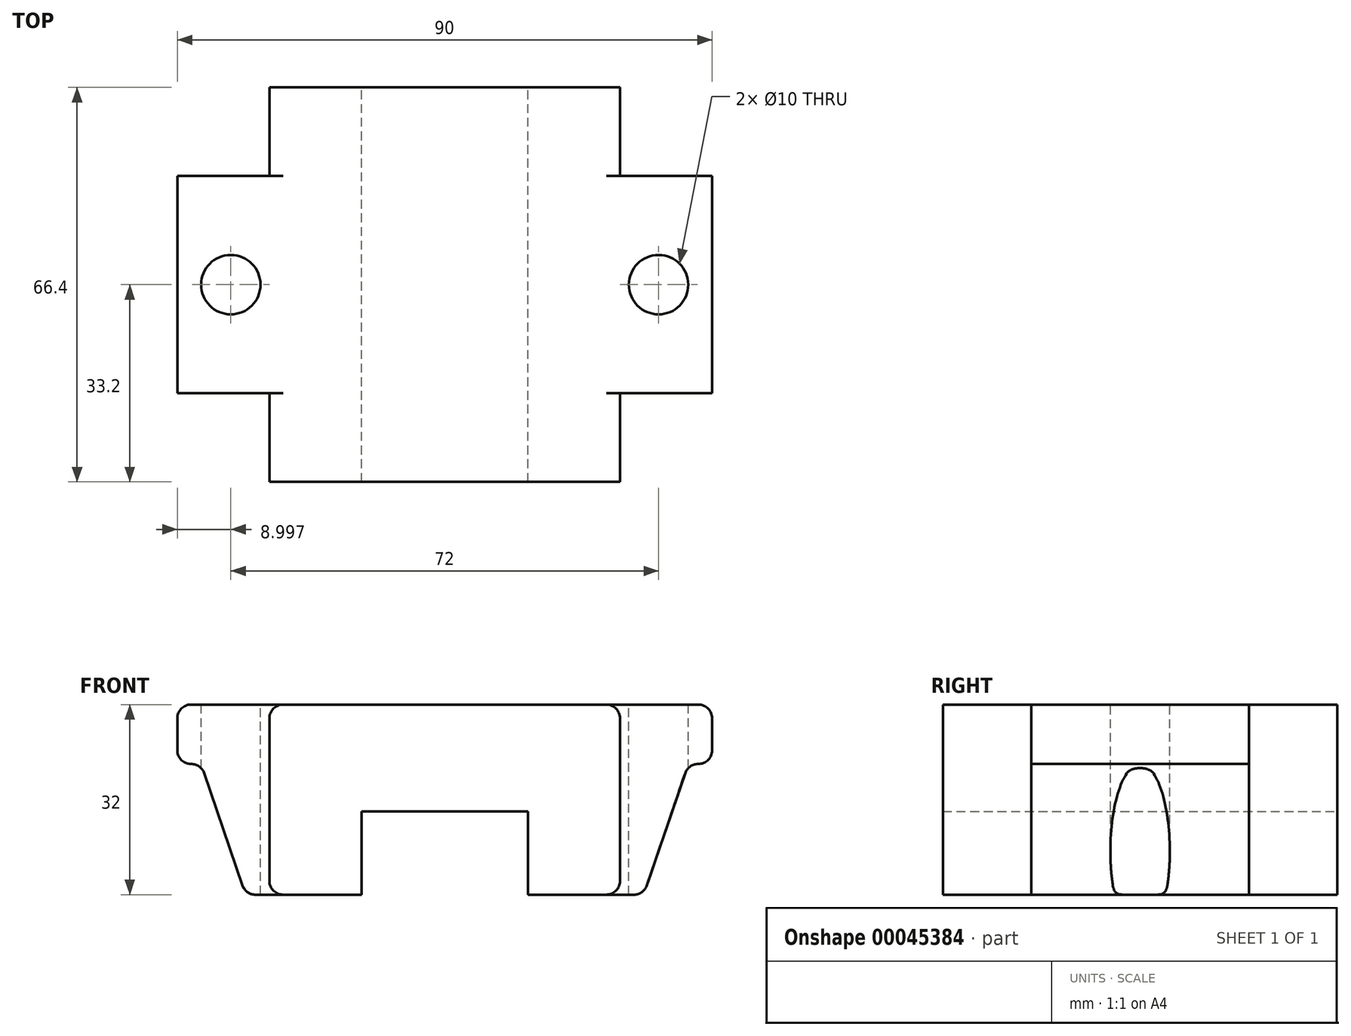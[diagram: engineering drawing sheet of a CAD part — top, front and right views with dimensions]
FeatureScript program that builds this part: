
annotation { "Feature Type Name" : "Feature", "Feature Type Description" : "" }
export const myFeature = defineFeature(function(context is Context, id is Id, definition is map)
    precondition{}
    {
        {
            var Q0;
            Q0=qCreatedBy(makeId("Front.planeOp"),FACE);
            var sketch = newSketch(context, id + "F0", { "sketchPlane" : qUnion([Q0])});
            skLineSegment(sketch, "E0.bottom", {"start": v(-43.91, 8.76) * mm, "end": v(46.09, 8.76) * mm});
            skLineSegment(sketch, "E0.top", {"start": v(-32.41, -23.24) * mm, "end": v(-12.91, -23.24) * mm});
            skLineSegment(sketch, "E0.left", {"start": v(-43.91, 8.76) * mm, "end": v(-43.91, -1.24) * mm});
            skLineSegment(sketch, "E0.right", {"start": v(46.09, 8.76) * mm, "end": v(46.09, -1.24) * mm});
            skLineSegment(sketch, "E1.top", {"start": v(-43.91, -1.24) * mm, "end": v(-39.91, -1.24) * mm});
            skLineSegment(sketch, "E2.bottom", {"start": v(-28.41, 8.76) * mm, "end": v(30.59, 8.76) * mm});
            skLineSegment(sketch, "E2.top", {"start": v(-28.41, -23.24) * mm, "end": v(-12.91, -23.24) * mm});
            skLineSegment(sketch, "E2.left", {"start": v(-28.41, 8.76) * mm, "end": v(-28.41, -23.24) * mm});
            skLineSegment(sketch, "E2.right", {"start": v(30.59, 8.76) * mm, "end": v(30.59, -23.24) * mm});
            skLineSegment(sketch, "E3.top", {"start": v(-12.91, -9.24) * mm, "end": v(15.09, -9.24) * mm});
            skLineSegment(sketch, "E3.left", {"start": v(-12.91, -23.24) * mm, "end": v(-12.91, -9.24) * mm});
            skLineSegment(sketch, "E3.right", {"start": v(15.09, -23.24) * mm, "end": v(15.09, -9.24) * mm});
            skLineSegment(sketch, "E4.trimOffspring", {"start": v(15.09, -23.24) * mm, "end": v(30.59, -23.24) * mm});
            skLineSegment(sketch, "E5.trimOffspring", {"start": v(15.09, -23.24) * mm, "end": v(34.59, -23.24) * mm});
            skLineSegment(sketch, "E6", {"start": v(-39.91, -1.24) * mm, "end": v(-32.41, -23.24) * mm});
            skLineSegment(sketch, "E7", {"start": v(34.59, -23.24) * mm, "end": v(42.09, -1.24) * mm});
            skLineSegment(sketch, "E8.trimOffspring", {"start": v(42.09, -1.24) * mm, "end": v(46.09, -1.24) * mm});
            skSolve(sketch);
        }
        {
            var Q0;
            Q0 = qSketchRegion(id + "F0", true);
            extrude(context, id + "F1", {"entities" : qUnion([Q0]), "depth" : 36.6 * mm});
        }
        {
            var Q0;
            Q0=makeQuery(id+"F1.opExtrude","CAP_FACE",FACE,{"disambiguationData":[OSD([sQuery(id+"F0.wireOp",EDGE,"E0.top"),sQuery(id+"F0.wireOp",EDGE,"E0.bottom"),sQuery(id+"F0.wireOp",EDGE,"E1.top"),sQuery(id+"F0.wireOp",EDGE,"E0.left"),sQuery(id+"F0.wireOp",EDGE,"E0.right"),sQuery(id+"F0.wireOp",EDGE,"E2.bottom"),sQuery(id+"F0.wireOp",EDGE,"E2.top"),sQuery(id+"F0.wireOp",EDGE,"E3.top"),sQuery(id+"F0.wireOp",EDGE,"E3.left"),sQuery(id+"F0.wireOp",EDGE,"E3.right"),sQuery(id+"F0.wireOp",EDGE,"E5.trimOffspring"),sQuery(id+"F0.wireOp",EDGE,"E6"),sQuery(id+"F0.wireOp",EDGE,"E7"),sQuery(id+"F0.wireOp",EDGE,"E8.trimOffspring")])],"isStart":true});
            var sketch = newSketch(context, id + "F2", { "sketchPlane" : qUnion([Q0])});
            skLineSegment(sketch, "E9.top", {"start": v(-30.59, 8.76) * mm, "end": v(28.41, 8.76) * mm});
            skLineSegment(sketch, "E9.left", {"start": v(-30.59, -23.24) * mm, "end": v(-30.59, 8.76) * mm});
            skLineSegment(sketch, "E9.right", {"start": v(28.41, -23.24) * mm, "end": v(28.41, 8.76) * mm});
            skLineSegment(sketch, "E10.top", {"start": v(-15.09, -9.24) * mm, "end": v(12.91, -9.24) * mm});
            skLineSegment(sketch, "E10.left", {"start": v(-15.09, -23.24) * mm, "end": v(-15.09, -9.24) * mm});
            skLineSegment(sketch, "E10.right", {"start": v(12.91, -23.24) * mm, "end": v(12.91, -9.24) * mm});
            skLineSegment(sketch, "E11.trimOffspring", {"start": v(12.91, -23.24) * mm, "end": v(28.41, -23.24) * mm});
            skLineSegment(sketch, "E12", {"start": v(-30.59, -23.24) * mm, "end": v(-15.09, -23.24) * mm});
            skSolve(sketch);
        }
        {
            var Q0;
            Q0 = qSketchRegion(id + "F2", true);
            extrude(context, id + "F3", {"entities" : qUnion([Q0]), "operationType" : NewBodyOperationType.ADD, "depth" : 14.9 * mm, "hasSecondDirection" : true, "secondDirectionOppositeDirection" : true, "secondDirectionDepth" : 51.5 * mm});
        }
        {
            var Q0;
            Q0=makeQuery(id+"F3.boolean.opBoolean","MERGE",FACE,{"derivedFrom":[makeQuery(id+"F1.opExtrude","SWEPT_FACE",FACE,{"disambiguationData":[OSD([sQuery(id+"F0.wireOp",EDGE,"E0.bottom"),sQuery(id+"F0.wireOp",EDGE,"E2.bottom")])]}),makeQuery(id+"F3.opExtrude","SWEPT_FACE",FACE,{"disambiguationData":[OSD([sQuery(id+"F2.wireOp",EDGE,"E9.top")])]})]});
            var sketch = newSketch(context, id + "F4", { "sketchPlane" : qUnion([Q0])});
            skCircle(sketch, "E13", {"center": v(-34.91, -18.3) * mm, "radius": 5 * mm});
            skCircle(sketch, "E14", {"center": v(37.09, -18.3) * mm, "radius": 5 * mm});
            skSolve(sketch);
        }
        {
            var Q0;
            Q0 = qSketchRegion(id + "F4", true);
            extrude(context, id + "F5", {"entities" : qUnion([Q0]), "operationType" : NewBodyOperationType.REMOVE, "endBound" : BoundingType.THROUGH_ALL, "oppositeDirection" : true, "depth" : 25 * mm});
        }
        {
            var Q0;
            {var subQ0=sQuery(id+"F0.wireOp",EDGE,"E6");var subQ1=sQuery(id+"F0.wireOp",EDGE,"E1.top");Q0=makeQuery(id+"F5.boolean.opBoolean","SPLIT",EDGE,{"disambiguationData":[TD([makeQuery(id+"F1.opExtrude","CAP_FACE",FACE,{"disambiguationData":[OSD([sQuery(id+"F0.wireOp",EDGE,"E0.top"),sQuery(id+"F0.wireOp",EDGE,"E0.bottom"),subQ1,sQuery(id+"F0.wireOp",EDGE,"E0.left"),sQuery(id+"F0.wireOp",EDGE,"E0.right"),sQuery(id+"F0.wireOp",EDGE,"E2.bottom"),sQuery(id+"F0.wireOp",EDGE,"E2.top"),sQuery(id+"F0.wireOp",EDGE,"E3.top"),sQuery(id+"F0.wireOp",EDGE,"E3.left"),sQuery(id+"F0.wireOp",EDGE,"E3.right"),sQuery(id+"F0.wireOp",EDGE,"E5.trimOffspring"),subQ0,sQuery(id+"F0.wireOp",EDGE,"E7"),sQuery(id+"F0.wireOp",EDGE,"E8.trimOffspring")])],"isStart":false})])],"derivedFrom":makeQuery(id+"F1.opExtrude","SWEPT_EDGE",EDGE,{"disambiguationData":[OSD([subQ1,subQ0])]})});}
            var Q1;
            Q1=makeQuery(id+"F1.opExtrude","SWEPT_EDGE",EDGE,{"disambiguationData":[OSD([sQuery(id+"F0.wireOp",EDGE,"E1.top"),sQuery(id+"F0.wireOp",EDGE,"E0.left")])]});
            var Q2;
            Q2=makeQuery(id+"F1.opExtrude","SWEPT_EDGE",EDGE,{"disambiguationData":[OSD([sQuery(id+"F0.wireOp",EDGE,"E0.bottom"),sQuery(id+"F0.wireOp",EDGE,"E0.left")])]});
            var Q3;
            {var subQ0=sQuery(id+"F0.wireOp",EDGE,"E6");var subQ1=sQuery(id+"F0.wireOp",EDGE,"E2.top");var subQ2=sQuery(id+"F0.wireOp",EDGE,"E0.top");Q3=makeQuery(id+"F5.boolean.opBoolean","SPLIT",EDGE,{"disambiguationData":[TD([makeQuery(id+"F1.opExtrude","CAP_FACE",FACE,{"disambiguationData":[OSD([subQ2,sQuery(id+"F0.wireOp",EDGE,"E0.bottom"),sQuery(id+"F0.wireOp",EDGE,"E1.top"),sQuery(id+"F0.wireOp",EDGE,"E0.left"),sQuery(id+"F0.wireOp",EDGE,"E0.right"),sQuery(id+"F0.wireOp",EDGE,"E2.bottom"),subQ1,sQuery(id+"F0.wireOp",EDGE,"E3.top"),sQuery(id+"F0.wireOp",EDGE,"E3.left"),sQuery(id+"F0.wireOp",EDGE,"E3.right"),sQuery(id+"F0.wireOp",EDGE,"E5.trimOffspring"),subQ0,sQuery(id+"F0.wireOp",EDGE,"E7"),sQuery(id+"F0.wireOp",EDGE,"E8.trimOffspring")])],"isStart":false})])],"derivedFrom":makeQuery(id+"F1.opExtrude","SWEPT_EDGE",EDGE,{"disambiguationData":[OSD([subQ2,subQ0])]})});}
            var Q4;
            {var subQ0=sQuery(id+"F0.wireOp",EDGE,"E6");var subQ1=sQuery(id+"F0.wireOp",EDGE,"E2.top");var subQ2=sQuery(id+"F0.wireOp",EDGE,"E0.top");Q4=makeQuery(id+"F5.boolean.opBoolean","SPLIT",EDGE,{"disambiguationData":[TD([makeQuery(id+"F1.opExtrude","CAP_FACE",FACE,{"disambiguationData":[OSD([subQ2,sQuery(id+"F0.wireOp",EDGE,"E0.bottom"),sQuery(id+"F0.wireOp",EDGE,"E1.top"),sQuery(id+"F0.wireOp",EDGE,"E0.left"),sQuery(id+"F0.wireOp",EDGE,"E0.right"),sQuery(id+"F0.wireOp",EDGE,"E2.bottom"),subQ1,sQuery(id+"F0.wireOp",EDGE,"E3.top"),sQuery(id+"F0.wireOp",EDGE,"E3.left"),sQuery(id+"F0.wireOp",EDGE,"E3.right"),sQuery(id+"F0.wireOp",EDGE,"E5.trimOffspring"),subQ0,sQuery(id+"F0.wireOp",EDGE,"E7"),sQuery(id+"F0.wireOp",EDGE,"E8.trimOffspring")])],"isStart":true})])],"derivedFrom":makeQuery(id+"F1.opExtrude","SWEPT_EDGE",EDGE,{"disambiguationData":[OSD([subQ2,subQ0])]})});}
            var Q5;
            {var subQ0=sQuery(id+"F2.wireOp",EDGE,"E9.right");var subQ1=sQuery(id+"F0.wireOp",EDGE,"E2.top");var subQ2=sQuery(id+"F0.wireOp",EDGE,"E0.top");var subQ3=sQuery(id+"F2.wireOp",EDGE,"E11.trimOffspring");Q5=makeQuery(id+"F3.boolean.opBoolean","SPLIT",EDGE,{"disambiguationData":[TD([makeQuery(id+"F3.opExtrude","CAP_FACE",FACE,{"disambiguationData":[OSD([sQuery(id+"F2.wireOp",EDGE,"E9.top"),sQuery(id+"F2.wireOp",EDGE,"E9.left"),subQ0,sQuery(id+"F2.wireOp",EDGE,"E10.top"),sQuery(id+"F2.wireOp",EDGE,"E10.left"),sQuery(id+"F2.wireOp",EDGE,"E10.right"),subQ3,sQuery(id+"F2.wireOp",EDGE,"E12")])],"isStart":true})])],"derivedFrom":makeQuery(id+"F3.opExtrude","SWEPT_EDGE",EDGE,{"disambiguationData":[OSD([subQ2,subQ1,subQ0,subQ3])]})});}
            var Q6;
            {var subQ0=sQuery(id+"F2.wireOp",EDGE,"E9.right");var subQ1=sQuery(id+"F0.wireOp",EDGE,"E2.top");var subQ2=sQuery(id+"F0.wireOp",EDGE,"E0.top");var subQ3=sQuery(id+"F2.wireOp",EDGE,"E11.trimOffspring");Q6=makeQuery(id+"F3.boolean.opBoolean","SPLIT",EDGE,{"disambiguationData":[TD([makeQuery(id+"F3.opExtrude","CAP_FACE",FACE,{"disambiguationData":[OSD([sQuery(id+"F2.wireOp",EDGE,"E9.top"),sQuery(id+"F2.wireOp",EDGE,"E9.left"),subQ0,sQuery(id+"F2.wireOp",EDGE,"E10.top"),sQuery(id+"F2.wireOp",EDGE,"E10.left"),sQuery(id+"F2.wireOp",EDGE,"E10.right"),subQ3,sQuery(id+"F2.wireOp",EDGE,"E12")])],"isStart":false})])],"derivedFrom":makeQuery(id+"F3.opExtrude","SWEPT_EDGE",EDGE,{"disambiguationData":[OSD([subQ2,subQ1,subQ0,subQ3])]})});}
            var Q7;
            {var subQ0=sQuery(id+"F0.wireOp",EDGE,"E2.bottom");var subQ1=sQuery(id+"F0.wireOp",EDGE,"E0.bottom");var subQ2=sQuery(id+"F2.wireOp",EDGE,"E9.right");var subQ3=sQuery(id+"F2.wireOp",EDGE,"E9.top");Q7=makeQuery(id+"F3.boolean.opBoolean","SPLIT",EDGE,{"disambiguationData":[TD([makeQuery(id+"F3.opExtrude","CAP_FACE",FACE,{"disambiguationData":[OSD([subQ3,sQuery(id+"F2.wireOp",EDGE,"E9.left"),subQ2,sQuery(id+"F2.wireOp",EDGE,"E10.top"),sQuery(id+"F2.wireOp",EDGE,"E10.left"),sQuery(id+"F2.wireOp",EDGE,"E10.right"),sQuery(id+"F2.wireOp",EDGE,"E11.trimOffspring"),sQuery(id+"F2.wireOp",EDGE,"E12")])],"isStart":true})])],"derivedFrom":makeQuery(id+"F3.opExtrude","SWEPT_EDGE",EDGE,{"disambiguationData":[OSD([subQ1,subQ0,subQ3,subQ2])]})});}
            var Q8;
            {var subQ0=sQuery(id+"F0.wireOp",EDGE,"E2.bottom");var subQ1=sQuery(id+"F0.wireOp",EDGE,"E0.bottom");var subQ2=sQuery(id+"F2.wireOp",EDGE,"E9.right");var subQ3=sQuery(id+"F2.wireOp",EDGE,"E9.top");Q8=makeQuery(id+"F3.boolean.opBoolean","SPLIT",EDGE,{"disambiguationData":[TD([makeQuery(id+"F3.opExtrude","CAP_FACE",FACE,{"disambiguationData":[OSD([subQ3,sQuery(id+"F2.wireOp",EDGE,"E9.left"),subQ2,sQuery(id+"F2.wireOp",EDGE,"E10.top"),sQuery(id+"F2.wireOp",EDGE,"E10.left"),sQuery(id+"F2.wireOp",EDGE,"E10.right"),sQuery(id+"F2.wireOp",EDGE,"E11.trimOffspring"),sQuery(id+"F2.wireOp",EDGE,"E12")])],"isStart":false})])],"derivedFrom":makeQuery(id+"F3.opExtrude","SWEPT_EDGE",EDGE,{"disambiguationData":[OSD([subQ1,subQ0,subQ3,subQ2])]})});}
            var Q9;
            {var subQ0=sQuery(id+"F0.wireOp",EDGE,"E2.bottom");var subQ1=sQuery(id+"F0.wireOp",EDGE,"E0.bottom");var subQ2=sQuery(id+"F2.wireOp",EDGE,"E9.left");var subQ3=sQuery(id+"F2.wireOp",EDGE,"E9.top");Q9=makeQuery(id+"F3.boolean.opBoolean","SPLIT",EDGE,{"disambiguationData":[TD([makeQuery(id+"F3.opExtrude","CAP_FACE",FACE,{"disambiguationData":[OSD([subQ3,subQ2,sQuery(id+"F2.wireOp",EDGE,"E9.right"),sQuery(id+"F2.wireOp",EDGE,"E10.top"),sQuery(id+"F2.wireOp",EDGE,"E10.left"),sQuery(id+"F2.wireOp",EDGE,"E10.right"),sQuery(id+"F2.wireOp",EDGE,"E11.trimOffspring"),sQuery(id+"F2.wireOp",EDGE,"E12")])],"isStart":false})])],"derivedFrom":makeQuery(id+"F3.opExtrude","SWEPT_EDGE",EDGE,{"disambiguationData":[OSD([subQ1,subQ0,subQ3,subQ2])]})});}
            var Q10;
            {var subQ0=sQuery(id+"F0.wireOp",EDGE,"E2.bottom");var subQ1=sQuery(id+"F0.wireOp",EDGE,"E0.bottom");var subQ2=sQuery(id+"F2.wireOp",EDGE,"E9.left");var subQ3=sQuery(id+"F2.wireOp",EDGE,"E9.top");Q10=makeQuery(id+"F3.boolean.opBoolean","SPLIT",EDGE,{"disambiguationData":[TD([makeQuery(id+"F3.opExtrude","CAP_FACE",FACE,{"disambiguationData":[OSD([subQ3,subQ2,sQuery(id+"F2.wireOp",EDGE,"E9.right"),sQuery(id+"F2.wireOp",EDGE,"E10.top"),sQuery(id+"F2.wireOp",EDGE,"E10.left"),sQuery(id+"F2.wireOp",EDGE,"E10.right"),sQuery(id+"F2.wireOp",EDGE,"E11.trimOffspring"),sQuery(id+"F2.wireOp",EDGE,"E12")])],"isStart":true})])],"derivedFrom":makeQuery(id+"F3.opExtrude","SWEPT_EDGE",EDGE,{"disambiguationData":[OSD([subQ1,subQ0,subQ3,subQ2])]})});}
            var Q11;
            Q11=makeQuery(id+"F1.opExtrude","SWEPT_EDGE",EDGE,{"disambiguationData":[OSD([sQuery(id+"F0.wireOp",EDGE,"E0.bottom"),sQuery(id+"F0.wireOp",EDGE,"E0.right")])]});
            var Q12;
            Q12=makeQuery(id+"F1.opExtrude","SWEPT_EDGE",EDGE,{"disambiguationData":[OSD([sQuery(id+"F0.wireOp",EDGE,"E0.right"),sQuery(id+"F0.wireOp",EDGE,"E8.trimOffspring")])]});
            var Q13;
            {var subQ0=sQuery(id+"F0.wireOp",EDGE,"E8.trimOffspring");var subQ1=sQuery(id+"F0.wireOp",EDGE,"E7");Q13=makeQuery(id+"F5.boolean.opBoolean","SPLIT",EDGE,{"disambiguationData":[TD([makeQuery(id+"F1.opExtrude","CAP_FACE",FACE,{"disambiguationData":[OSD([sQuery(id+"F0.wireOp",EDGE,"E0.top"),sQuery(id+"F0.wireOp",EDGE,"E0.bottom"),sQuery(id+"F0.wireOp",EDGE,"E1.top"),sQuery(id+"F0.wireOp",EDGE,"E0.left"),sQuery(id+"F0.wireOp",EDGE,"E0.right"),sQuery(id+"F0.wireOp",EDGE,"E2.bottom"),sQuery(id+"F0.wireOp",EDGE,"E2.top"),sQuery(id+"F0.wireOp",EDGE,"E3.top"),sQuery(id+"F0.wireOp",EDGE,"E3.left"),sQuery(id+"F0.wireOp",EDGE,"E3.right"),sQuery(id+"F0.wireOp",EDGE,"E5.trimOffspring"),sQuery(id+"F0.wireOp",EDGE,"E6"),subQ1,subQ0])],"isStart":false})])],"derivedFrom":makeQuery(id+"F1.opExtrude","SWEPT_EDGE",EDGE,{"disambiguationData":[OSD([subQ1,subQ0])]})});}
            var Q14;
            {var subQ0=sQuery(id+"F0.wireOp",EDGE,"E7");var subQ1=sQuery(id+"F0.wireOp",EDGE,"E5.trimOffspring");Q14=makeQuery(id+"F5.boolean.opBoolean","SPLIT",EDGE,{"disambiguationData":[TD([makeQuery(id+"F1.opExtrude","CAP_FACE",FACE,{"disambiguationData":[OSD([sQuery(id+"F0.wireOp",EDGE,"E0.top"),sQuery(id+"F0.wireOp",EDGE,"E0.bottom"),sQuery(id+"F0.wireOp",EDGE,"E1.top"),sQuery(id+"F0.wireOp",EDGE,"E0.left"),sQuery(id+"F0.wireOp",EDGE,"E0.right"),sQuery(id+"F0.wireOp",EDGE,"E2.bottom"),sQuery(id+"F0.wireOp",EDGE,"E2.top"),sQuery(id+"F0.wireOp",EDGE,"E3.top"),sQuery(id+"F0.wireOp",EDGE,"E3.left"),sQuery(id+"F0.wireOp",EDGE,"E3.right"),subQ1,sQuery(id+"F0.wireOp",EDGE,"E6"),subQ0,sQuery(id+"F0.wireOp",EDGE,"E8.trimOffspring")])],"isStart":false})])],"derivedFrom":makeQuery(id+"F1.opExtrude","SWEPT_EDGE",EDGE,{"disambiguationData":[OSD([subQ1,subQ0])]})});}
            var Q15;
            {var subQ0=sQuery(id+"F0.wireOp",EDGE,"E7");var subQ1=sQuery(id+"F0.wireOp",EDGE,"E5.trimOffspring");Q15=makeQuery(id+"F5.boolean.opBoolean","SPLIT",EDGE,{"disambiguationData":[TD([makeQuery(id+"F1.opExtrude","CAP_FACE",FACE,{"disambiguationData":[OSD([sQuery(id+"F0.wireOp",EDGE,"E0.top"),sQuery(id+"F0.wireOp",EDGE,"E0.bottom"),sQuery(id+"F0.wireOp",EDGE,"E1.top"),sQuery(id+"F0.wireOp",EDGE,"E0.left"),sQuery(id+"F0.wireOp",EDGE,"E0.right"),sQuery(id+"F0.wireOp",EDGE,"E2.bottom"),sQuery(id+"F0.wireOp",EDGE,"E2.top"),sQuery(id+"F0.wireOp",EDGE,"E3.top"),sQuery(id+"F0.wireOp",EDGE,"E3.left"),sQuery(id+"F0.wireOp",EDGE,"E3.right"),subQ1,sQuery(id+"F0.wireOp",EDGE,"E6"),subQ0,sQuery(id+"F0.wireOp",EDGE,"E8.trimOffspring")])],"isStart":true})])],"derivedFrom":makeQuery(id+"F1.opExtrude","SWEPT_EDGE",EDGE,{"disambiguationData":[OSD([subQ1,subQ0])]})});}
            var Q16;
            {var subQ0=sQuery(id+"F0.wireOp",EDGE,"E5.trimOffspring");var subQ1=sQuery(id+"F2.wireOp",EDGE,"E12");var subQ2=sQuery(id+"F2.wireOp",EDGE,"E9.left");Q16=makeQuery(id+"F3.boolean.opBoolean","SPLIT",EDGE,{"disambiguationData":[TD([makeQuery(id+"F3.opExtrude","CAP_FACE",FACE,{"disambiguationData":[OSD([sQuery(id+"F2.wireOp",EDGE,"E9.top"),subQ2,sQuery(id+"F2.wireOp",EDGE,"E9.right"),sQuery(id+"F2.wireOp",EDGE,"E10.top"),sQuery(id+"F2.wireOp",EDGE,"E10.left"),sQuery(id+"F2.wireOp",EDGE,"E10.right"),sQuery(id+"F2.wireOp",EDGE,"E11.trimOffspring"),subQ1])],"isStart":true})])],"derivedFrom":makeQuery(id+"F3.opExtrude","SWEPT_EDGE",EDGE,{"disambiguationData":[OSD([subQ0,subQ2,subQ1])]})});}
            var Q17;
            {var subQ0=sQuery(id+"F0.wireOp",EDGE,"E5.trimOffspring");var subQ1=sQuery(id+"F2.wireOp",EDGE,"E12");var subQ2=sQuery(id+"F2.wireOp",EDGE,"E9.left");Q17=makeQuery(id+"F3.boolean.opBoolean","SPLIT",EDGE,{"disambiguationData":[TD([makeQuery(id+"F3.opExtrude","CAP_FACE",FACE,{"disambiguationData":[OSD([sQuery(id+"F2.wireOp",EDGE,"E9.top"),subQ2,sQuery(id+"F2.wireOp",EDGE,"E9.right"),sQuery(id+"F2.wireOp",EDGE,"E10.top"),sQuery(id+"F2.wireOp",EDGE,"E10.left"),sQuery(id+"F2.wireOp",EDGE,"E10.right"),sQuery(id+"F2.wireOp",EDGE,"E11.trimOffspring"),subQ1])],"isStart":false})])],"derivedFrom":makeQuery(id+"F3.opExtrude","SWEPT_EDGE",EDGE,{"disambiguationData":[OSD([subQ0,subQ2,subQ1])]})});}
            var Q18;
            {var subQ0=sQuery(id+"F0.wireOp",EDGE,"E8.trimOffspring");var subQ1=sQuery(id+"F0.wireOp",EDGE,"E7");Q18=makeQuery(id+"F5.boolean.opBoolean","SPLIT",EDGE,{"disambiguationData":[TD([makeQuery(id+"F1.opExtrude","CAP_FACE",FACE,{"disambiguationData":[OSD([sQuery(id+"F0.wireOp",EDGE,"E0.top"),sQuery(id+"F0.wireOp",EDGE,"E0.bottom"),sQuery(id+"F0.wireOp",EDGE,"E1.top"),sQuery(id+"F0.wireOp",EDGE,"E0.left"),sQuery(id+"F0.wireOp",EDGE,"E0.right"),sQuery(id+"F0.wireOp",EDGE,"E2.bottom"),sQuery(id+"F0.wireOp",EDGE,"E2.top"),sQuery(id+"F0.wireOp",EDGE,"E3.top"),sQuery(id+"F0.wireOp",EDGE,"E3.left"),sQuery(id+"F0.wireOp",EDGE,"E3.right"),sQuery(id+"F0.wireOp",EDGE,"E5.trimOffspring"),sQuery(id+"F0.wireOp",EDGE,"E6"),subQ1,subQ0])],"isStart":true})])],"derivedFrom":makeQuery(id+"F1.opExtrude","SWEPT_EDGE",EDGE,{"disambiguationData":[OSD([subQ1,subQ0])]})});}
            var Q19;
            {var subQ0=sQuery(id+"F0.wireOp",EDGE,"E6");var subQ1=sQuery(id+"F0.wireOp",EDGE,"E1.top");Q19=makeQuery(id+"F5.boolean.opBoolean","SPLIT",EDGE,{"disambiguationData":[TD([makeQuery(id+"F1.opExtrude","CAP_FACE",FACE,{"disambiguationData":[OSD([sQuery(id+"F0.wireOp",EDGE,"E0.top"),sQuery(id+"F0.wireOp",EDGE,"E0.bottom"),subQ1,sQuery(id+"F0.wireOp",EDGE,"E0.left"),sQuery(id+"F0.wireOp",EDGE,"E0.right"),sQuery(id+"F0.wireOp",EDGE,"E2.bottom"),sQuery(id+"F0.wireOp",EDGE,"E2.top"),sQuery(id+"F0.wireOp",EDGE,"E3.top"),sQuery(id+"F0.wireOp",EDGE,"E3.left"),sQuery(id+"F0.wireOp",EDGE,"E3.right"),sQuery(id+"F0.wireOp",EDGE,"E5.trimOffspring"),subQ0,sQuery(id+"F0.wireOp",EDGE,"E7"),sQuery(id+"F0.wireOp",EDGE,"E8.trimOffspring")])],"isStart":true})])],"derivedFrom":makeQuery(id+"F1.opExtrude","SWEPT_EDGE",EDGE,{"disambiguationData":[OSD([subQ1,subQ0])]})});}
            fillet(context, id + "F6", {"entities" : qUnion([Q0, Q1, Q2, Q3, Q4, Q5, Q6, Q7, Q8, Q9, Q10, Q11, Q12, Q13, Q14, Q15, Q16, Q17, Q18, Q19]), "radius" : 2.3 * mm, "tangentPropagation" : true, "allowEdgeOverflow" : false});
        }
    });
